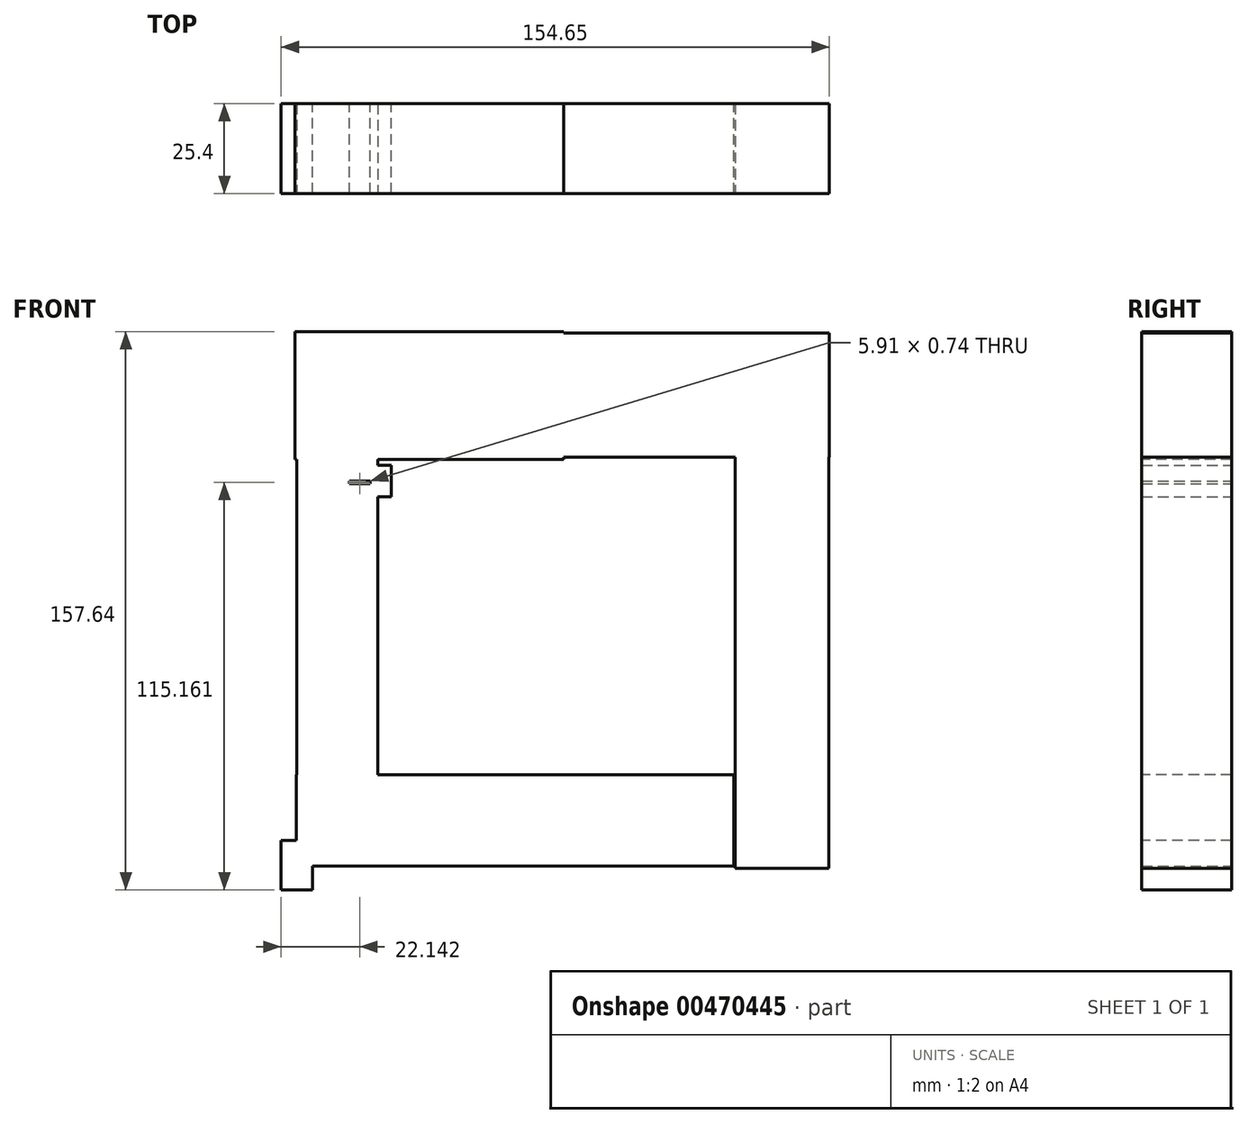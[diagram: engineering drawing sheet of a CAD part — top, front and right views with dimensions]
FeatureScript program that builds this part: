
annotation { "Feature Type Name" : "Feature", "Feature Type Description" : "" }
export const myFeature = defineFeature(function(context is Context, id is Id, definition is map)
    precondition{}
    {
        {
            var Q0;
            Q0=qCreatedBy(makeId("Front.planeOp"),FACE);
            var sketch = newSketch(context, id + "F0", { "sketchPlane" : qUnion([Q0])});
            skLineSegment(sketch, "E0.bottom", {"start": v(-75.8, 75.9) * mm, "end": v(0, 75.9) * mm});
            skLineSegment(sketch, "E0.top", {"start": v(-75.8, 39.9) * mm, "end": v(0, 39.9) * mm});
            skLineSegment(sketch, "E0.left", {"start": v(-75.8, 75.9) * mm, "end": v(-75.8, 39.9) * mm});
            skLineSegment(sketch, "E0.right", {"start": v(0, 75.9) * mm, "end": v(0, 39.9) * mm});
            skSolve(sketch);
        }
        {
            var Q0;
            Q0=makeQuery(id+"F0.imprint","IMPRINT",FACE,{"disambiguationData":[TD([[makeQuery(id+"F0.imprint","IMPRINT",EDGE,{"derivedFrom":sQuery(id+"F0.wireOp",EDGE,"E0.bottom")}),-1.0]])]});
            extrude(context, id + "F1", {"entities" : qUnion([Q0]), "depth" : 25.4 * mm});
        }
        {
            var Q0;
            Q0=qCreatedBy(makeId("Front.planeOp"),FACE);
            var sketch = newSketch(context, id + "F2", { "sketchPlane" : qUnion([Q0])});
            skLineSegment(sketch, "E1.bottom", {"start": v(74.95, 75.5) * mm, "end": v(0, 75.5) * mm});
            skLineSegment(sketch, "E1.top", {"start": v(74.95, 40.43) * mm, "end": v(0, 40.43) * mm});
            skLineSegment(sketch, "E1.left", {"start": v(74.95, 75.5) * mm, "end": v(74.95, 40.43) * mm});
            skLineSegment(sketch, "E1.right", {"start": v(0, 75.5) * mm, "end": v(0, 40.43) * mm});
            skLineSegment(sketch, "E2.bottom", {"start": v(0, 40.43) * mm, "end": v(25.5, 40.43) * mm});
            skLineSegment(sketch, "E2.top", {"start": v(0, 33.05) * mm, "end": v(25.5, 33.05) * mm});
            skLineSegment(sketch, "E2.left", {"start": v(0, 40.43) * mm, "end": v(0, 33.05) * mm});
            skLineSegment(sketch, "E2.right", {"start": v(25.5, 40.43) * mm, "end": v(25.5, 33.05) * mm});
            skLineSegment(sketch, "E3.bottom", {"start": v(25.5, 33.05) * mm, "end": v(0, 33.05) * mm});
            skLineSegment(sketch, "E3.top", {"start": v(25.5, 40.43) * mm, "end": v(0, 40.43) * mm});
            skLineSegment(sketch, "E3.left", {"start": v(25.5, 33.05) * mm, "end": v(25.5, 40.43) * mm});
            skLineSegment(sketch, "E3.right", {"start": v(0, 33.05) * mm, "end": v(0, 40.43) * mm});
            skLineSegment(sketch, "E4.bottom", {"start": v(153.57, 45.97) * mm, "end": v(155.79, 45.97) * mm});
            skLineSegment(sketch, "E4.top", {"start": v(153.57, 45.6) * mm, "end": v(155.79, 45.6) * mm});
            skLineSegment(sketch, "E4.left", {"start": v(153.57, 45.97) * mm, "end": v(153.57, 45.6) * mm});
            skLineSegment(sketch, "E4.right", {"start": v(155.79, 45.97) * mm, "end": v(155.79, 45.6) * mm});
            skSolve(sketch);
        }
        {
            var Q0;
            Q0=qCreatedBy(makeId("Front.planeOp"),FACE);
            var sketch = newSketch(context, id + "F3", { "sketchPlane" : qUnion([Q0])});
            skLineSegment(sketch, "E5.bottom", {"start": v(-54.6, 33.8) * mm, "end": v(-60.51, 33.8) * mm});
            skLineSegment(sketch, "E5.top", {"start": v(-54.6, 33.05) * mm, "end": v(-60.51, 33.05) * mm});
            skLineSegment(sketch, "E5.left", {"start": v(-54.6, 33.8) * mm, "end": v(-54.6, 33.05) * mm});
            skLineSegment(sketch, "E5.right", {"start": v(-60.51, 33.8) * mm, "end": v(-60.51, 33.05) * mm});
            skPoint(sketch, "E5.middle", {"position": v(-57.56, 33.42) * mm});
            skLineSegment(sketch, "E6.bottom", {"start": v(-60.51, 29.36) * mm, "end": v(-48.7, 29.36) * mm});
            skLineSegment(sketch, "E6.top", {"start": v(-60.51, 38.22) * mm, "end": v(-48.7, 38.22) * mm});
            skLineSegment(sketch, "E6.left", {"start": v(-60.51, 29.36) * mm, "end": v(-60.51, 38.22) * mm});
            skLineSegment(sketch, "E6.right", {"start": v(-48.7, 29.36) * mm, "end": v(-48.7, 38.22) * mm});
            skPoint(sketch, "E6.middle", {"position": v(-54.6, 33.8) * mm});
            skLineSegment(sketch, "E7.bottom", {"start": v(-70.85, -67.71) * mm, "end": v(-79.7, -67.71) * mm});
            skLineSegment(sketch, "E7.top", {"start": v(-70.85, -81.74) * mm, "end": v(-79.7, -81.74) * mm});
            skLineSegment(sketch, "E7.left", {"start": v(-70.85, -67.71) * mm, "end": v(-70.85, -81.74) * mm});
            skLineSegment(sketch, "E7.right", {"start": v(-79.7, -67.71) * mm, "end": v(-79.7, -81.74) * mm});
            skPoint(sketch, "E7.middle", {"position": v(-75.28, -74.73) * mm});
            skLineSegment(sketch, "E8.bottom", {"start": v(-75.28, -74.73) * mm, "end": v(-52.4, -74.73) * mm});
            skLineSegment(sketch, "E8.top", {"start": v(-75.28, 59.63) * mm, "end": v(-52.4, 59.63) * mm});
            skLineSegment(sketch, "E8.left", {"start": v(-75.28, -74.73) * mm, "end": v(-75.28, 59.63) * mm});
            skLineSegment(sketch, "E8.right", {"start": v(-52.4, -74.73) * mm, "end": v(-52.4, 59.63) * mm});
            skPoint(sketch, "E8.middle", {"position": v(-63.83, -7.55) * mm});
            skSolve(sketch);
        }
        {
            var Q0;
            Q0 = qSketchRegion(id + "F3", true);
            extrude(context, id + "F4", {"entities" : qUnion([Q0]), "operationType" : NewBodyOperationType.ADD, "depth" : 25.4 * mm});
        }
        {
            var Q0;
            Q0=makeQuery(id+"F2.imprint","IMPRINT",FACE,{"disambiguationData":[TD([[makeQuery(id+"F2.imprint","IMPRINT",EDGE,{"derivedFrom":sQuery(id+"F2.wireOp",EDGE,"E1.bottom")}),1.0]])]});
            extrude(context, id + "F5", {"entities" : qUnion([Q0]), "operationType" : NewBodyOperationType.ADD, "depth" : 25.4 * mm});
        }
        {
            var Q0;
            Q0=qCreatedBy(makeId("Front.planeOp"),FACE);
            var sketch = newSketch(context, id + "F6", { "sketchPlane" : qUnion([Q0])});
            skLineSegment(sketch, "E9.bottom", {"start": v(74.84, 41.25) * mm, "end": v(48.44, 41.25) * mm});
            skLineSegment(sketch, "E9.top", {"start": v(74.84, -75.61) * mm, "end": v(48.44, -75.61) * mm});
            skLineSegment(sketch, "E9.left", {"start": v(74.84, 41.25) * mm, "end": v(74.84, -75.61) * mm});
            skLineSegment(sketch, "E9.right", {"start": v(48.44, 41.25) * mm, "end": v(48.44, -75.61) * mm});
            skSolve(sketch);
        }
        {
            var Q0;
            Q0 = qSketchRegion(id + "F6", true);
            extrude(context, id + "F7", {"entities" : qUnion([Q0]), "operationType" : NewBodyOperationType.ADD, "depth" : 25.4 * mm});
        }
        {
            var Q0;
            Q0=qCreatedBy(makeId("Front.planeOp"),FACE);
            var sketch = newSketch(context, id + "F8", { "sketchPlane" : qUnion([Q0])});
            skLineSegment(sketch, "E10.bottom", {"start": v(48.05, -49.22) * mm, "end": v(-75.4, -49.22) * mm});
            skLineSegment(sketch, "E10.top", {"start": v(48.05, -74.92) * mm, "end": v(-75.4, -74.92) * mm});
            skLineSegment(sketch, "E10.left", {"start": v(48.05, -49.22) * mm, "end": v(48.05, -74.92) * mm});
            skLineSegment(sketch, "E10.right", {"start": v(-75.4, -49.22) * mm, "end": v(-75.4, -74.92) * mm});
            skSolve(sketch);
        }
        {
            var Q0;
            Q0 = qSketchRegion(id + "F8", true);
            extrude(context, id + "F9", {"entities" : qUnion([Q0]), "operationType" : NewBodyOperationType.ADD, "depth" : 25.4 * mm});
        }
    });
